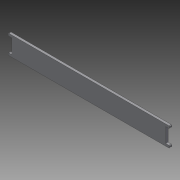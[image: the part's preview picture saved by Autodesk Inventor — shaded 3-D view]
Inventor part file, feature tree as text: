
AUTODESK INVENTOR PART (.ipt)
format: ipt  version: 2015 (Build 190159000, 159)  size: 98,816 bytes
history: native  units: mm
features: extrude x1
ambient origin geometry x8: Origin, YZ Plane, XZ Plane, XY Plane, X Axis, Y Axis, Z Axis, Center Point
bodies: Solid1 (feature_tree)
feature tree (1):
  extrude  "Extrusion1"  Depth=3.0mm
